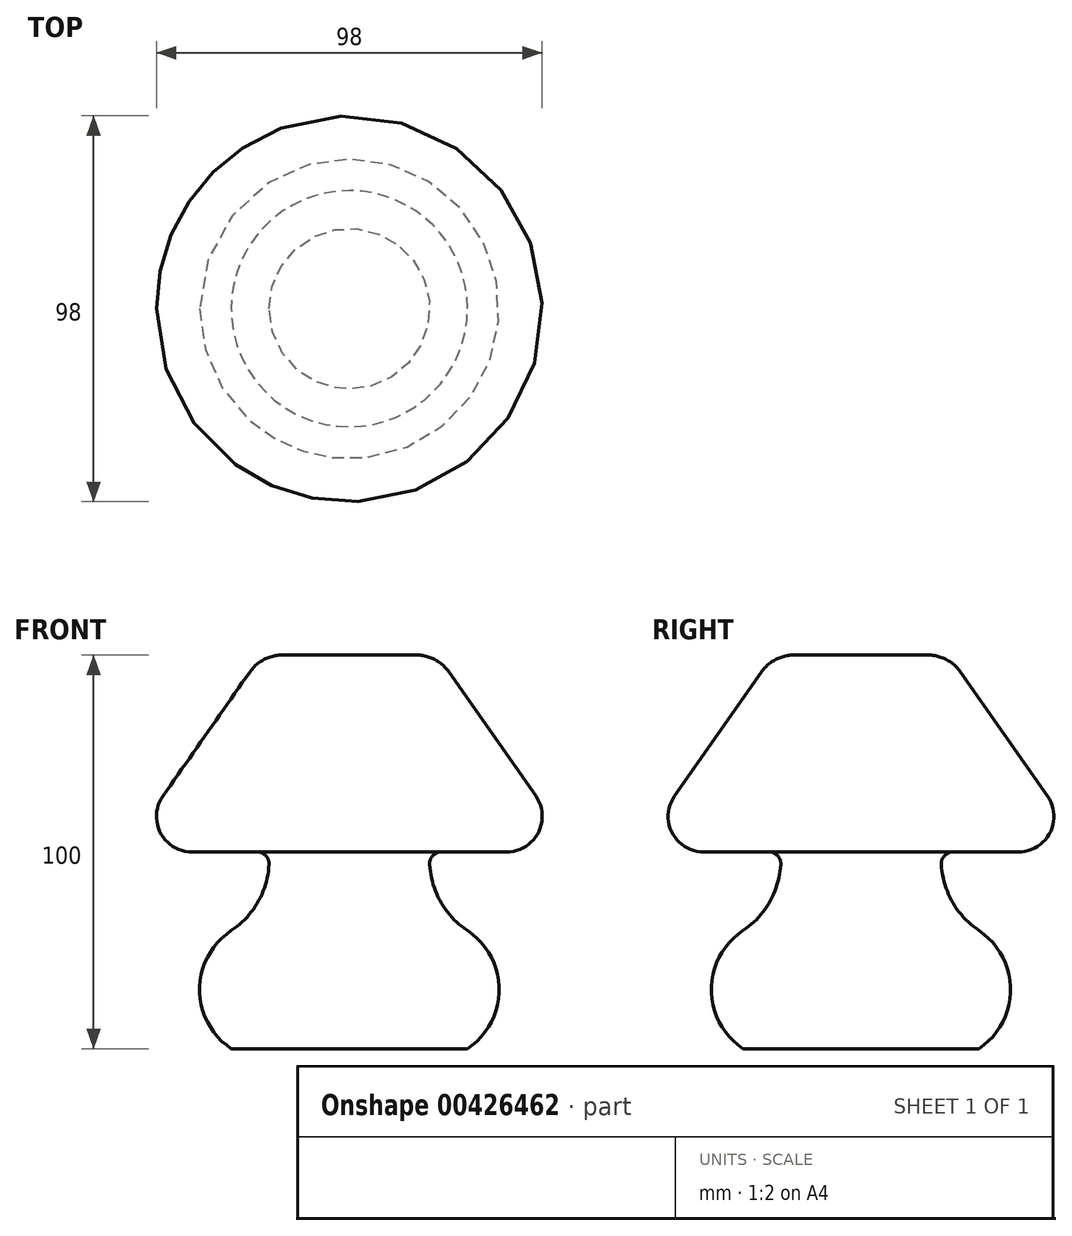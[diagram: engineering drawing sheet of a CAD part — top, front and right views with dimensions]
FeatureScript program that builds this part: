
annotation { "Feature Type Name" : "Feature", "Feature Type Description" : "" }
export const myFeature = defineFeature(function(context is Context, id is Id, definition is map)
    precondition{}
    {
        {
            var Q0;
            Q0=qCreatedBy(makeId("Front.planeOp"),FACE);
            var sketch = newSketch(context, id + "F0", { "sketchPlane" : qUnion([Q0])});
            skLineSegment(sketch, "E0", {"start": v(0, 0) * mm, "end": v(30, 0) * mm});
            skArc(sketch, "E1", {"start": v(30, 0) * mm, "mid": v(38.03, 15) * mm, "end": v(30, 30) * mm});
            skArc(sketch, "E2", {"start": v(20.46, 50) * mm, "mid": v(22.47, 38.69) * mm, "end": v(30, 30) * mm});
            skLineSegment(sketch, "E3", {"start": v(20.46, 50) * mm, "end": v(40, 50) * mm});
            skLineSegment(sketch, "E4", {"start": v(47.37, 64.16) * mm, "end": v(25.26, 95.74) * mm});
            skLineSegment(sketch, "E5", {"start": v(17.07, 100) * mm, "end": v(0, 100) * mm});
            skArc(sketch, "E6.filletArc", {"start": v(40, 50) * mm, "mid": v(47.98, 54.84) * mm, "end": v(47.37, 64.16) * mm});
            skPoint(sketch, "E7.visualSharp", {"position": v(22.28, 100) * mm});
            skArc(sketch, "E7.filletArc", {"start": v(25.26, 95.74) * mm, "mid": v(21.7, 98.87) * mm, "end": v(17.07, 100) * mm});
            skLineSegment(sketch, "E8", {"start": v(0, 0) * mm, "end": v(0, 126.12) * mm, "construction": true});
            skPoint(sketch, "E9.orphan", {"position": v(0, 50) * mm});
            skLineSegment(sketch, "E10", {"start": v(0, 100) * mm, "end": v(0, 0) * mm});
            skSolve(sketch);
        }
        {
            var Q0;
            Q0=makeQuery(id+"F0.imprint","IMPRINT",FACE,{"disambiguationData":[TD([[makeQuery(id+"F0.imprint","IMPRINT",EDGE,{"derivedFrom":sQuery(id+"F0.wireOp",EDGE,"E0")}),1.0]])]});
            var Q1;
            Q1=sQuery(id+"F0.wireOp",EDGE,"E8");
            revolve(context, id + "F1", {"entities" : qUnion([Q0]), "axis" : qUnion([Q1]), "revolveType" : RevolveType.FULL});
        }
        {
            var Q0;
            Q0=makeQuery(id+"F1.opRevolve","SWEPT_EDGE",EDGE,{"disambiguationData":[OSD([sQuery(id+"F0.wireOp",EDGE,"E2"),sQuery(id+"F0.wireOp",EDGE,"E3")])]});
            fillet(context, id + "F2", {"entities" : qUnion([Q0]), "radius" : 3 * mm, "tangentPropagation" : true, "allowEdgeOverflow" : false});
        }
    });
